# Revit family: Faucet-Lavatory-KOHLER-Composed-K-73060W_1
name_source: partatom
category: Plumbing Fixtures
revit_build: Autodesk Revit 2017 (Build: 20160225_1515(x64)
units: mm (PartAtom-declared; Revit-internal decimal feet)

## family parameters
Cut with Voids When Loaded = No
Host = Face
OmniClass Number = 23.31.11.00
OmniClass Title = Faucets
Part Type = Normal
Room Calculation Point = No
Round Connector Dimension = Use Diameter
Shared = No

## types (2) — shared parameters
ADA Compliant = No
Assembly Code = D2010
CW Connection = Yes
Cold Water Inlet = Cold Water Inlet
Date Modified = 06/26/2020
Default Elevation = 36"
Drain Included = Yes
Finish = Kohler-Metal-CP-Polished_Chrome
Flow Rate = 1 GPM
HW Connection = Yes
Handle Clearance = 3"
Height = 4 9/16"
Hot Water Inlet = Hot Water Inlet
Length = 5 15/16"
Manufacturer = KOHLER Co.
Master Format 2014 = 22 41 39
Master Format 2014 Name = Residential Faucets, Supplies, and Trim
Material = solid brass construction
Pressure = 43.51 psi
Product Documentation Link = https://resources.kohler.com
Product Name = Composed
Product Page URL = https://www.kohler.co.uk
Spout Reach = 5 15/16"
URL = https://www.kohler.co.uk
Vent Connection = No
Waste Connection = No
Waste Water Outlet = Waste Water Outlet
WaterSense Certified = No

## per-type parameters (varying)
| type | Cross Handle | Description | Dist | Lever Handle | Model | Type |
| Cross Handle, CP-Polished Chrome | Yes | 3-hole basin mixer, cross handle | 1 1/2" | No | K-73060W-3-CP | 1 |
| Lever Handle, CP-Polished Chrome | No | 3-hole basin mixer, lever handle | 0" | Yes | K-73060W-4-CP | 2 |

## geometry (parser evidence)
native form markers: Sweep x6
no freeform markers — native parametric forms only
